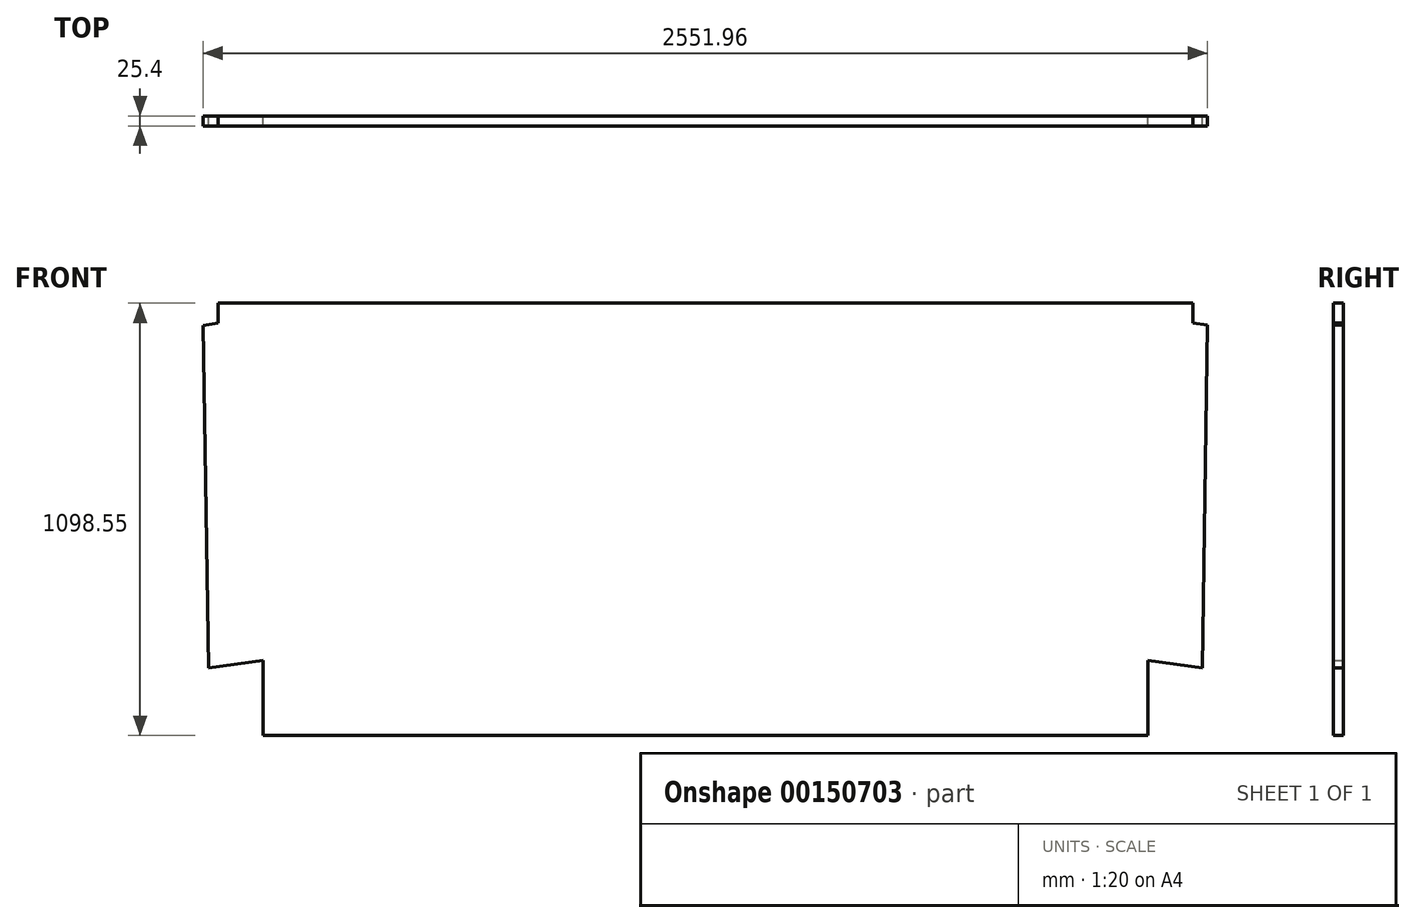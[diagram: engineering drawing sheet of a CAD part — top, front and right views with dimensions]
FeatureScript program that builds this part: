
annotation { "Feature Type Name" : "Feature", "Feature Type Description" : "" }
export const myFeature = defineFeature(function(context is Context, id is Id, definition is map)
    precondition{}
    {
        {
            var Q0;
            Q0=qCreatedBy(makeId("Front.planeOp"),FACE);
            var sketch = newSketch(context, id + "F0", { "sketchPlane" : qUnion([Q0])});
            skLineSegment(sketch, "E0", {"start": v(0, 0) * mm, "end": v(2247.9, 0) * mm});
            skLineSegment(sketch, "E1", {"start": v(0, 0) * mm, "end": v(0, 190.5) * mm});
            skLineSegment(sketch, "E2", {"start": v(2247.9, 0) * mm, "end": v(2247.9, 190.5) * mm});
            skLineSegment(sketch, "E3", {"start": v(2362.2, 1098.55) * mm, "end": v(-114.3, 1098.55) * mm});
            skLineSegment(sketch, "E4", {"start": v(-114.3, 1098.55) * mm, "end": v(-114.3, 1047.75) * mm});
            skLineSegment(sketch, "E5", {"start": v(2362.2, 1098.55) * mm, "end": v(2362.2, 1047.75) * mm});
            skLineSegment(sketch, "E6", {"start": v(2362.2, 1047.75) * mm, "end": v(2400, 1042.99) * mm});
            skLineSegment(sketch, "E7", {"start": v(2247.9, 190.5) * mm, "end": v(2386.37, 172.04) * mm});
            skLineSegment(sketch, "E8", {"start": v(2386.37, 172.04) * mm, "end": v(2400, 1042.99) * mm});
            skLineSegment(sketch, "E9", {"start": v(-114.3, 1047.75) * mm, "end": v(-151.96, 1042) * mm});
            skLineSegment(sketch, "E10", {"start": v(0, 190.5) * mm, "end": v(-138.47, 172.04) * mm});
            skLineSegment(sketch, "E11", {"start": v(-151.96, 1042) * mm, "end": v(-138.47, 172.04) * mm});
            skSolve(sketch);
        }
        {
            var Q0;
            Q0 = qSketchRegion(id + "F0", true);
            extrude(context, id + "F1", {"entities" : qUnion([Q0]), "depth" : 25.4 * mm});
        }
    });
